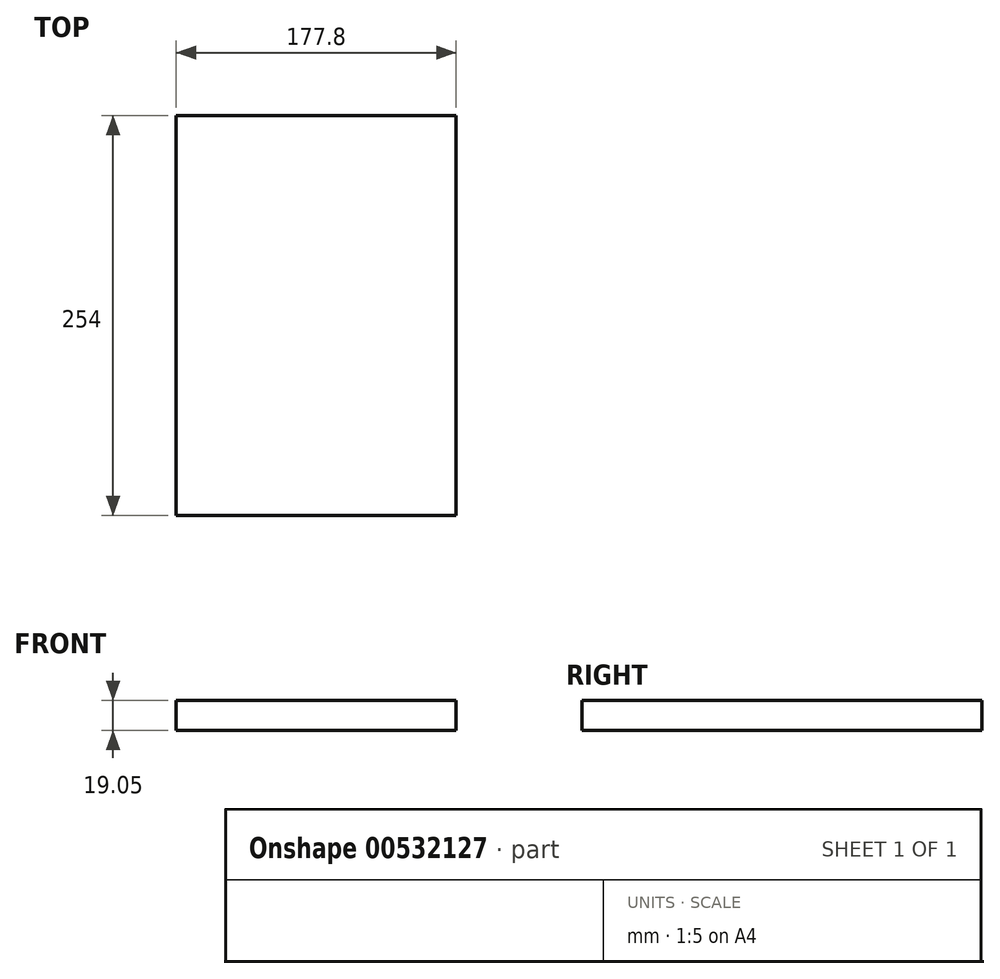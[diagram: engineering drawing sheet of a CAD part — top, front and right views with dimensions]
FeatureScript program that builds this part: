
annotation { "Feature Type Name" : "Feature", "Feature Type Description" : "" }
export const myFeature = defineFeature(function(context is Context, id is Id, definition is map)
    precondition{}
    {
        {
            var Q0;
            Q0=qCreatedBy(makeId("Top.planeOp"),FACE);
            var sketch = newSketch(context, id + "F0", { "sketchPlane" : qUnion([Q0])});
            skLineSegment(sketch, "E0.bottom", {"start": v(88.9, -127) * mm, "end": v(-88.9, -127) * mm});
            skLineSegment(sketch, "E0.top", {"start": v(88.9, 127) * mm, "end": v(-88.9, 127) * mm});
            skLineSegment(sketch, "E0.left", {"start": v(88.9, -127) * mm, "end": v(88.9, 127) * mm});
            skLineSegment(sketch, "E0.right", {"start": v(-88.9, -127) * mm, "end": v(-88.9, 127) * mm});
            skPoint(sketch, "E0.middle", {"position": v(0, 0) * mm});
            skSolve(sketch);
        }
        {
            var Q0;
            Q0 = qSketchRegion(id + "F0", true);
            extrude(context, id + "F1", {"entities" : qUnion([Q0]), "depth" : 19.05 * mm, "offsetDistance" : 25.4 * mm});
        }
    });
